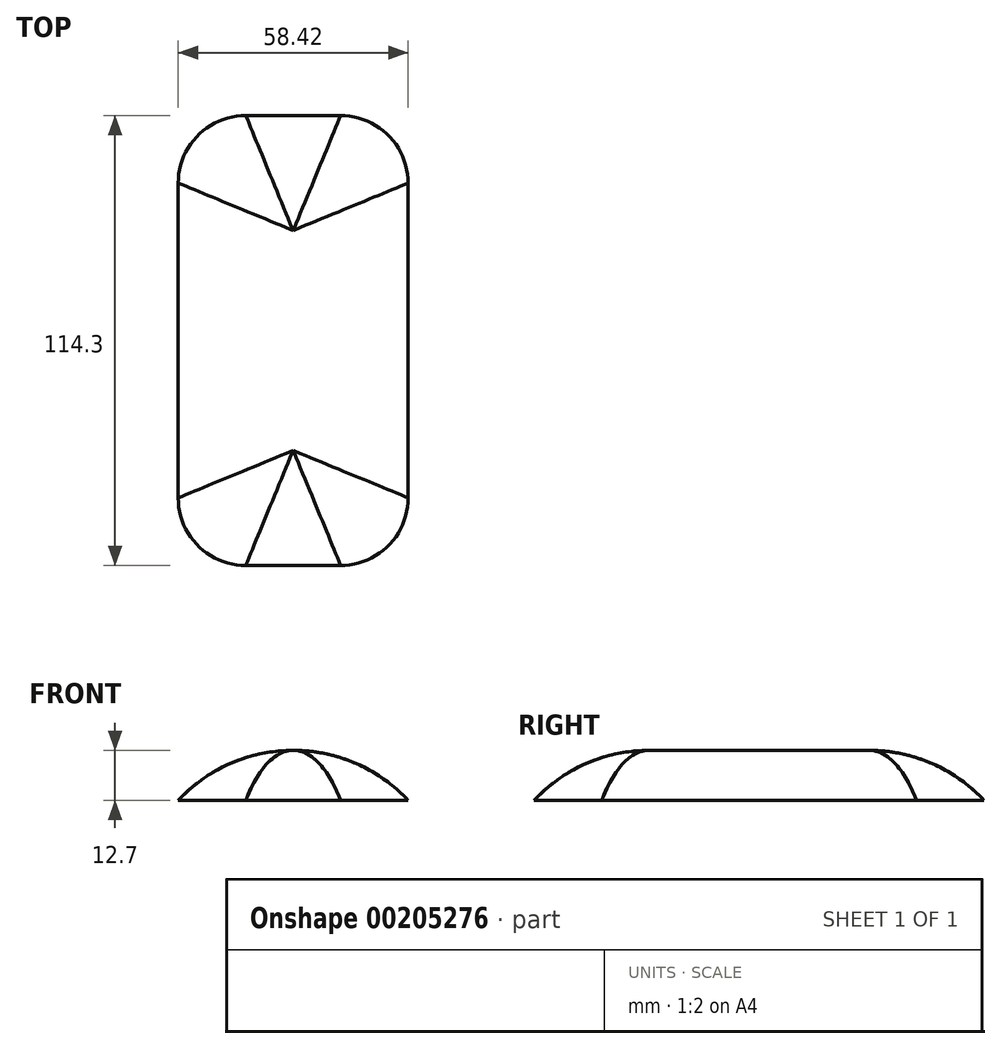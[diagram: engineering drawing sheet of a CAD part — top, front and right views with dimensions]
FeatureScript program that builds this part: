
annotation { "Feature Type Name" : "Feature", "Feature Type Description" : "" }
export const myFeature = defineFeature(function(context is Context, id is Id, definition is map)
    precondition{}
    {
        {
            var Q0;
            Q0=qCreatedBy(makeId("Top.planeOp"),FACE);
            var sketch = newSketch(context, id + "F0", { "sketchPlane" : qUnion([Q0])});
            skLineSegment(sketch, "E0.bottom", {"start": v(-83.02, 52) * mm, "end": v(-24.6, 52) * mm});
            skLineSegment(sketch, "E0.top", {"start": v(-83.02, -62.3) * mm, "end": v(-24.6, -62.3) * mm});
            skLineSegment(sketch, "E0.left", {"start": v(-83.02, 52) * mm, "end": v(-83.02, -62.3) * mm});
            skLineSegment(sketch, "E0.right", {"start": v(-24.6, 52) * mm, "end": v(-24.6, -62.3) * mm});
            skSolve(sketch);
        }
        {
            var Q0;
            Q0=makeQuery(id+"F0.imprint","IMPRINT",FACE,{"disambiguationData":[TD([[makeQuery(id+"F0.imprint","IMPRINT",EDGE,{"derivedFrom":sQuery(id+"F0.wireOp",EDGE,"E0.bottom")}),-1.0]])]});
            extrude(context, id + "F1", {"entities" : qUnion([Q0]), "depth" : 12.7 * mm});
        }
        {
            var Q0;
            Q0=makeQuery(id+"F1.opExtrude","SWEPT_EDGE",EDGE,{"disambiguationData":[OSD([sQuery(id+"F0.wireOp",EDGE,"E0.top"),sQuery(id+"F0.wireOp",EDGE,"E0.left")])]});
            var Q1;
            Q1=makeQuery(id+"F1.opExtrude","SWEPT_EDGE",EDGE,{"disambiguationData":[OSD([sQuery(id+"F0.wireOp",EDGE,"E0.top"),sQuery(id+"F0.wireOp",EDGE,"E0.right")])]});
            var Q2;
            Q2=makeQuery(id+"F1.opExtrude","SWEPT_EDGE",EDGE,{"disambiguationData":[OSD([sQuery(id+"F0.wireOp",EDGE,"E0.bottom"),sQuery(id+"F0.wireOp",EDGE,"E0.right")])]});
            var Q3;
            Q3=makeQuery(id+"F1.opExtrude","SWEPT_EDGE",EDGE,{"disambiguationData":[OSD([sQuery(id+"F0.wireOp",EDGE,"E0.bottom"),sQuery(id+"F0.wireOp",EDGE,"E0.left")])]});
            fillet(context, id + "F2", {"entities" : qUnion([Q0, Q1, Q2, Q3]), "radius" : 17.17 * mm, "tangentPropagation" : true, "allowEdgeOverflow" : false});
        }
        {
            var Q0;
            Q0=makeQuery(id+"F1.opExtrude","CAP_EDGE",EDGE,{"disambiguationData":[OSD([sQuery(id+"F0.wireOp",EDGE,"E0.left")])],"isStart":false});
            fillet(context, id + "F3", {"entities" : qUnion([Q0]), "radius" : 39.86 * mm, "tangentPropagation" : true, "allowEdgeOverflow" : false});
        }
    });
